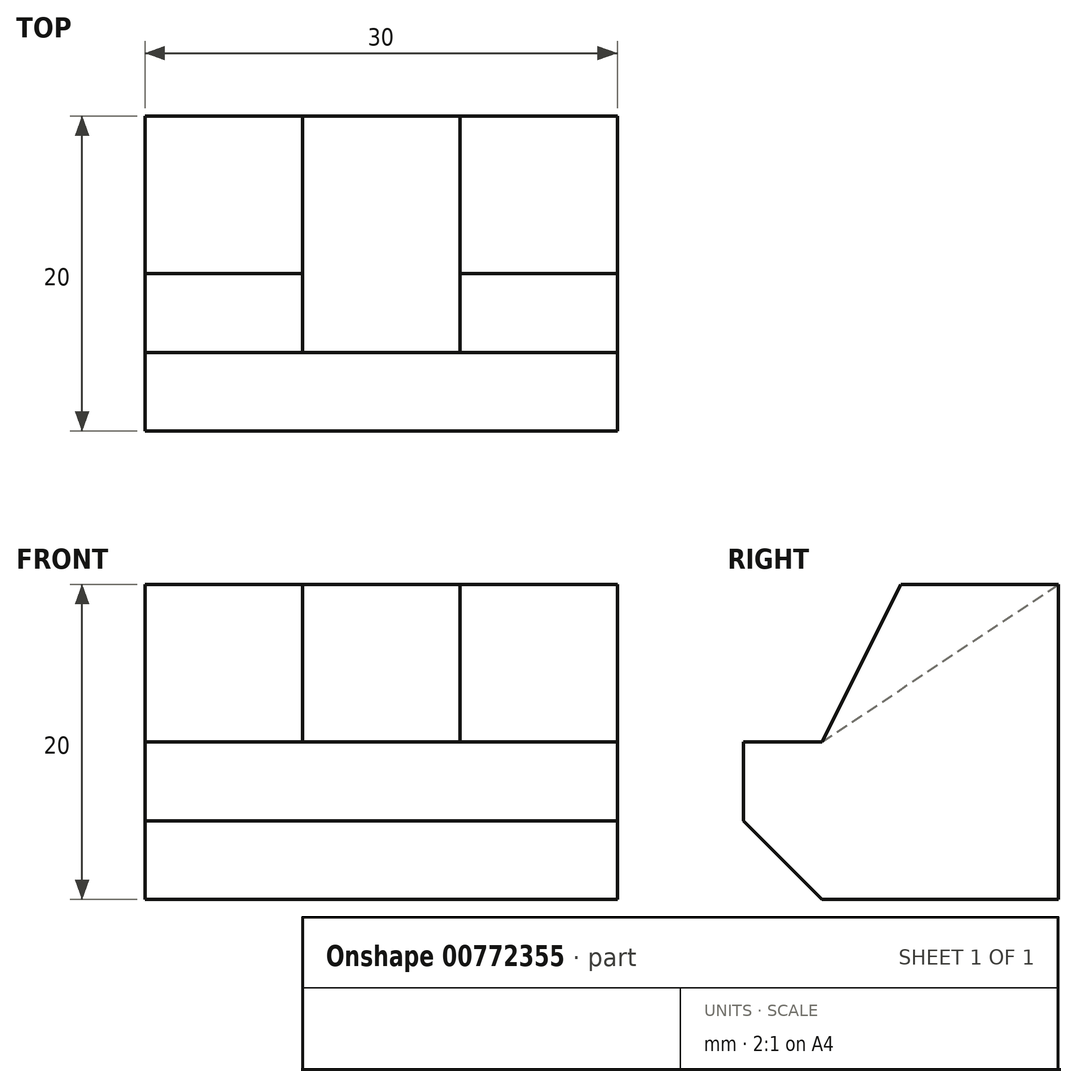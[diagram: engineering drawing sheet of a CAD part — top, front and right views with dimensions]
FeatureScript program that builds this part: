
annotation { "Feature Type Name" : "Feature", "Feature Type Description" : "" }
export const myFeature = defineFeature(function(context is Context, id is Id, definition is map)
    precondition{}
    {
        {
            var Q0;
            Q0=qCreatedBy(makeId("Right.planeOp"),FACE);
            var sketch = newSketch(context, id + "F0", { "sketchPlane" : qUnion([Q0])});
            skLineSegment(sketch, "E0", {"start": v(0, 0) * mm, "end": v(0, 20) * mm});
            skLineSegment(sketch, "E1", {"start": v(0, 20) * mm, "end": v(-10, 20) * mm});
            skLineSegment(sketch, "E2", {"start": v(-10, 20) * mm, "end": v(-15, 10) * mm});
            skLineSegment(sketch, "E3", {"start": v(-15, 10) * mm, "end": v(-20, 10) * mm});
            skLineSegment(sketch, "E4", {"start": v(-20, 10) * mm, "end": v(-20, 5) * mm});
            skLineSegment(sketch, "E5", {"start": v(-20, 5) * mm, "end": v(-15, 0) * mm});
            skLineSegment(sketch, "E6", {"start": v(-15, 0) * mm, "end": v(0, 0) * mm});
            skLineSegment(sketch, "E7", {"start": v(-15, 10) * mm, "end": v(0, 20) * mm});
            skSolve(sketch);
        }
        {
            var Q0;
            Q0=makeQuery(id+"F0.imprint","IMPRINT",FACE,{"disambiguationData":[TD([[makeQuery(id+"F0.imprint","IMPRINT",EDGE,{"derivedFrom":sQuery(id+"F0.wireOp",EDGE,"E0")}),1.0]])]});
            var Q1;
            Q1=makeQuery(id+"F0.imprint","IMPRINT",FACE,{"disambiguationData":[TD([[makeQuery(id+"F0.imprint","IMPRINT",EDGE,{"derivedFrom":sQuery(id+"F0.wireOp",EDGE,"E1")}),1.0]])]});
            extrude(context, id + "F1", {"entities" : qUnion([Q0, Q1]), "endBound" : BoundingType.SYMMETRIC, "depth" : 30 * mm, "offsetDistance" : 25 * mm});
        }
        {
            var Q0;
            Q0=makeQuery(id+"F0.imprint","IMPRINT",FACE,{"disambiguationData":[TD([[makeQuery(id+"F0.imprint","IMPRINT",EDGE,{"derivedFrom":sQuery(id+"F0.wireOp",EDGE,"E1")}),1.0]])]});
            extrude(context, id + "F2", {"entities" : qUnion([Q0]), "operationType" : NewBodyOperationType.REMOVE, "endBound" : BoundingType.SYMMETRIC, "oppositeDirection" : true, "depth" : 10 * mm, "offsetDistance" : 25 * mm});
        }
    });
